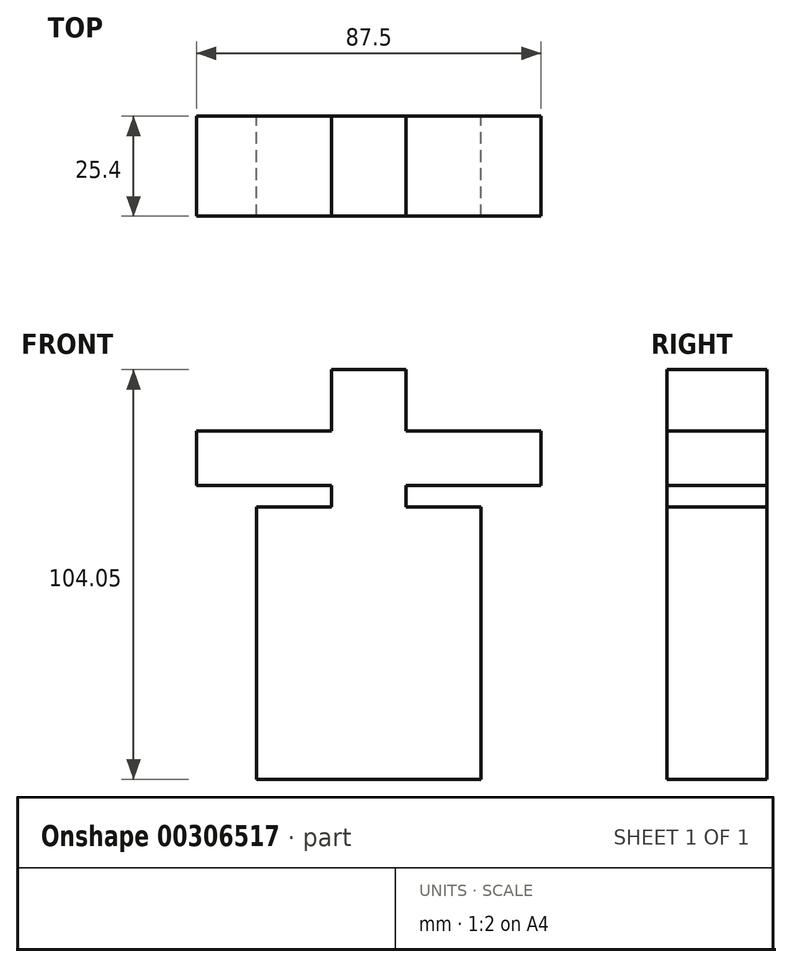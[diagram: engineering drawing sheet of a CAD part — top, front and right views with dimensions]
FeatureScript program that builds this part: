
annotation { "Feature Type Name" : "Feature", "Feature Type Description" : "" }
export const myFeature = defineFeature(function(context is Context, id is Id, definition is map)
    precondition{}
    {
        {
            var Q0;
            Q0=qCreatedBy(makeId("Front.planeOp"),FACE);
            var sketch = newSketch(context, id + "F0", { "sketchPlane" : qUnion([Q0])});
            skLineSegment(sketch, "E0.bottom", {"start": v(28.5, 34.61) * mm, "end": v(-28.5, 34.61) * mm});
            skLineSegment(sketch, "E0.top", {"start": v(28.5, -34.61) * mm, "end": v(-28.5, -34.61) * mm});
            skLineSegment(sketch, "E0.left", {"start": v(28.5, 34.61) * mm, "end": v(28.5, -34.61) * mm});
            skLineSegment(sketch, "E0.right", {"start": v(-28.5, 34.61) * mm, "end": v(-28.5, -34.61) * mm});
            skPoint(sketch, "E0.middle", {"position": v(0, 0) * mm});
            skLineSegment(sketch, "E1.bottom", {"start": v(9.5, 69.44) * mm, "end": v(-9.5, 69.44) * mm});
            skLineSegment(sketch, "E1.top", {"start": v(9.5, -0.22) * mm, "end": v(-9.5, -0.22) * mm});
            skLineSegment(sketch, "E1.left", {"start": v(9.5, 69.44) * mm, "end": v(9.5, -0.22) * mm});
            skLineSegment(sketch, "E1.right", {"start": v(-9.5, 69.44) * mm, "end": v(-9.5, -0.22) * mm});
            skPoint(sketch, "E1.middle", {"position": v(0, 34.61) * mm});
            skLineSegment(sketch, "E2.bottom", {"start": v(-43.75, 53.9) * mm, "end": v(43.75, 53.9) * mm});
            skLineSegment(sketch, "E2.top", {"start": v(-43.75, 40.08) * mm, "end": v(43.75, 40.08) * mm});
            skLineSegment(sketch, "E2.left", {"start": v(-43.75, 53.9) * mm, "end": v(-43.75, 40.08) * mm});
            skLineSegment(sketch, "E2.right", {"start": v(43.75, 53.9) * mm, "end": v(43.75, 40.08) * mm});
            skPoint(sketch, "E2.middle", {"position": v(0, 46.99) * mm});
            skSolve(sketch);
        }
        {
            var Q0;
            {var subQ0=sQuery(id+"F0.wireOp",EDGE,"E1.bottom");Q0=makeQuery(id+"F0.imprint","IMPRINT",FACE,{"disambiguationData":[TD([[makeQuery(id+"F0.imprint","IMPRINT",EDGE,{"derivedFrom":subQ0}),1.0]])]});}
            var Q1;
            {var subQ0=sQuery(id+"F0.wireOp",EDGE,"E2.bottom");var subQ1=sQuery(id+"F0.wireOp",EDGE,"E1.left");var subQ2=makeQuery(id+"F0.imprint","INTERSECT",VERTEX,{"derivedFrom":[subQ1,subQ0]});Q1=makeQuery(id+"F0.imprint","IMPRINT",FACE,{"disambiguationData":[TD([[makeQuery(id+"F0.imprint","IMPRINT",EDGE,{"disambiguationData":[TD([[subQ2,-1.0]])],"derivedFrom":subQ1}),-1.0]])]});}
            var Q2;
            {var subQ5=sQuery(id+"F0.wireOp",EDGE,"E2.left");Q2=makeQuery(id+"F0.imprint","IMPRINT",FACE,{"disambiguationData":[TD([[makeQuery(id+"F0.imprint","IMPRINT",EDGE,{"derivedFrom":subQ5}),1.0]])]});}
            var Q3;
            {var subQ5=sQuery(id+"F0.wireOp",EDGE,"E2.right");Q3=makeQuery(id+"F0.imprint","IMPRINT",FACE,{"disambiguationData":[TD([[makeQuery(id+"F0.imprint","IMPRINT",EDGE,{"derivedFrom":subQ5}),-1.0]])]});}
            var Q4;
            {var subQ0=sQuery(id+"F0.wireOp",EDGE,"E1.left");var subQ1=sQuery(id+"F0.wireOp",EDGE,"E0.bottom");var subQ2=makeQuery(id+"F0.imprint","INTERSECT",VERTEX,{"derivedFrom":[subQ1,subQ0]});Q4=makeQuery(id+"F0.imprint","IMPRINT",FACE,{"disambiguationData":[TD([[makeQuery(id+"F0.imprint","IMPRINT",EDGE,{"disambiguationData":[TD([[subQ2,-1.0]])],"derivedFrom":subQ1}),-1.0]])]});}
            var Q5;
            {var subQ5=sQuery(id+"F0.wireOp",EDGE,"E1.top");Q5=makeQuery(id+"F0.imprint","IMPRINT",FACE,{"disambiguationData":[TD([[makeQuery(id+"F0.imprint","IMPRINT",EDGE,{"derivedFrom":subQ5}),-1.0]])]});}
            var Q6;
            Q6=makeQuery(id+"F0.imprint","IMPRINT",FACE,{"disambiguationData":[TD([[makeQuery(id+"F0.imprint","IMPRINT",EDGE,{"derivedFrom":sQuery(id+"F0.wireOp",EDGE,"E0.top")}),-1.0]])]});
            extrude(context, id + "F1", {"entities" : qUnion([Q0, Q1, Q2, Q3, Q4, Q5, Q6]), "depth" : 25.4 * mm});
        }
    });
